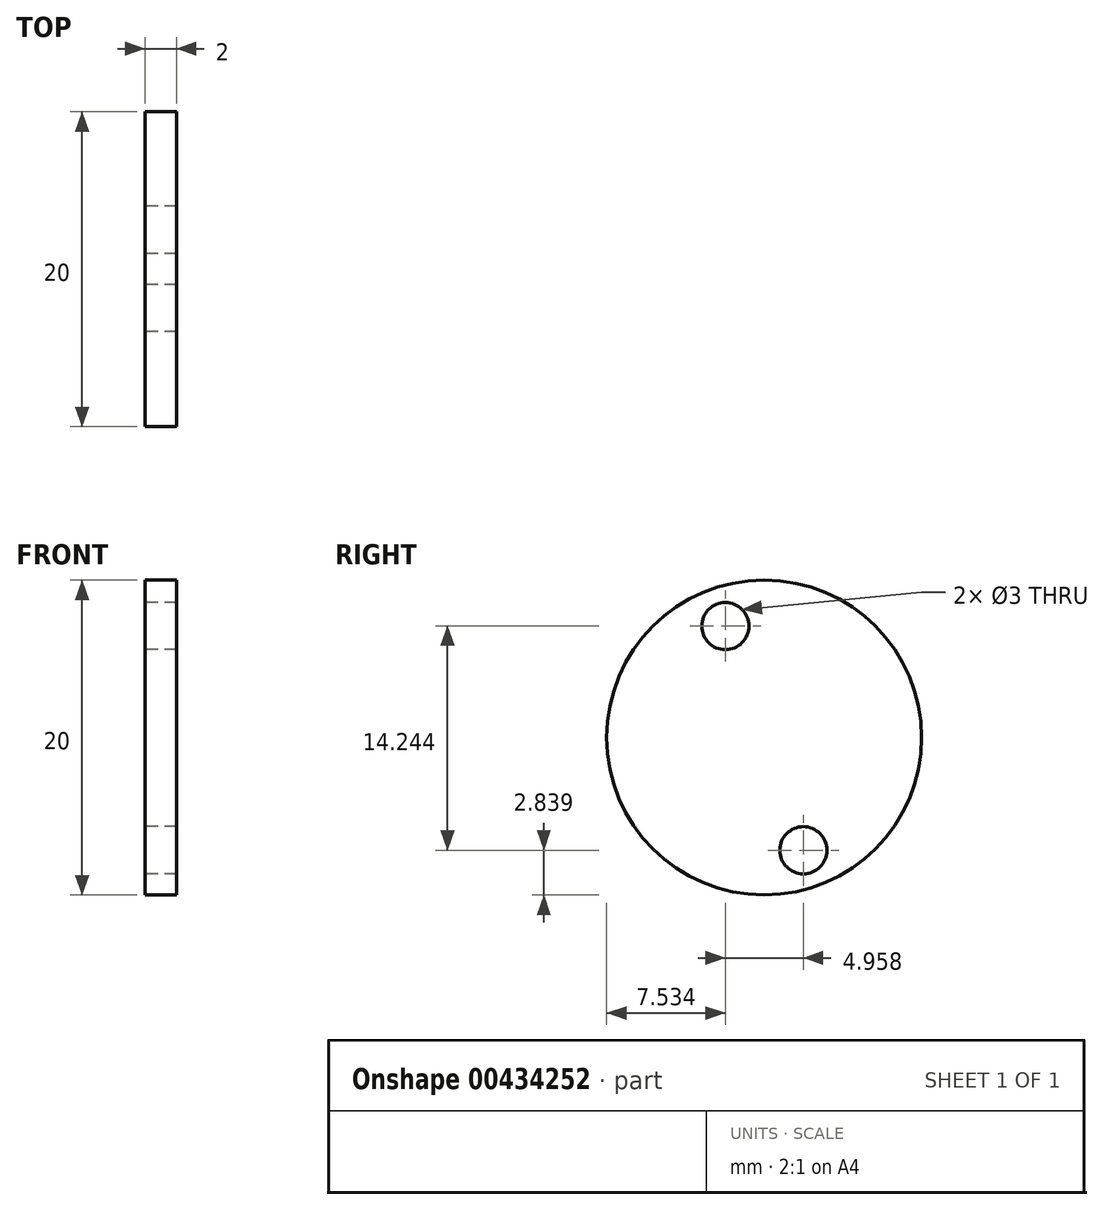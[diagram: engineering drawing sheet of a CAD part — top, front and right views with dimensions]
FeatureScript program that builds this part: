
annotation { "Feature Type Name" : "Feature", "Feature Type Description" : "" }
export const myFeature = defineFeature(function(context is Context, id is Id, definition is map)
    precondition{}
    {
        {
            var Q0;
            Q0=qCreatedBy(makeId("Right.planeOp"),FACE);
            var sketch = newSketch(context, id + "F0", { "sketchPlane" : qUnion([Q0])});
            skCircle(sketch, "E0", {"center": v(0, 0) * mm, "radius": 10 * mm});
            skCircle(sketch, "E1", {"center": v(-2.47, 7.08) * mm, "radius": 1.5 * mm});
            skCircle(sketch, "E2", {"center": v(2.5, -7.16) * mm, "radius": 1.5 * mm});
            skSolve(sketch);
        }
        {
            var Q0;
            Q0 = qSketchRegion(id + "F0", true);
            extrude(context, id + "F1", {"entities" : qUnion([Q0]), "depth" : 2 * mm});
        }
    });
